FCSTD DOCUMENT  (FreeCAD 0.18R16131 (Git))
Label: SomeFaceJustLayer
License: All rights reserved
LicenseURL: http://en.wikipedia.org/wiki/All_rights_reserved
objects: Sketcher::SketchObject×1
note: 1 computed .brp shape members not serialized (recipe doc carries the construction recipe); baked Part::Feature solids carry a one-line shape summary decoded from their .brp

FEATURE [Sketcher::SketchObject] Sketch
  sketch-geometry (11):
    g0: LineSegment StartX=-16.4573 StartY=10.8332 StartZ=0 EndX=-15.7927 EndY=19.2026 EndZ=0
    g1: LineSegment StartX=-15.7927 StartY=19.2026 StartZ=0 EndX=-22.7085 EndY=23.9628 EndZ=0
    g2: LineSegment StartX=-22.7085 StartY=23.9628 StartZ=0 EndX=-30.2889 EndY=20.3537 EndZ=0
    g3: LineSegment StartX=-30.2889 StartY=20.3537 StartZ=0 EndX=-30.9535 EndY=11.9843 EndZ=0
    g4: LineSegment StartX=-30.9535 StartY=11.9843 StartZ=0 EndX=-24.0377 EndY=7.22407 EndZ=0
    g5: LineSegment StartX=-24.0377 StartY=7.22407 StartZ=0 EndX=-16.4573 EndY=10.8332 EndZ=0
    g6: Circle [constr] CenterX=-23.3731 CenterY=15.5935 CenterZ=0 NormalX=0 NormalY=0 NormalZ=1 AngleXU=0 Radius=8.39573
    g7: ArcOfCircle CenterX=-40.1686 CenterY=13.6448 CenterZ=0 NormalX=0 NormalY=0 NormalZ=1 AngleXU=0 Radius=15.6279 StartAngle=1.5708 EndAngle=4.71239
    g8: ArcOfCircle CenterX=6.8872 CenterY=13.6448 CenterZ=0 NormalX=0 NormalY=0 NormalZ=1 AngleXU=0 Radius=15.6279 StartAngle=4.71239 EndAngle=7.85398
    g9: LineSegment StartX=-40.1686 StartY=-1.98313 StartZ=0 EndX=6.8872 EndY=-1.98313 EndZ=0
    g10: LineSegment StartX=-40.1686 StartY=29.2728 StartZ=0 EndX=6.8872 EndY=29.2728 EndZ=0
  constraints (19):
    c: Coincident(g0,g1)
    c: Coincident(g1,g2)
    c: Coincident(g2,g3)
    c: Coincident(g3,g4)
    c: Coincident(g4,g5)
    c: Coincident(g5,g0)
    c: Equal(g0, g1-g5) x5
    c: PointOnObject(g0,g6)
    c: PointOnObject(g1,g6)
    c: PointOnObject(g2,g6)
    c: PointOnObject(g3,g6)
    c: PointOnObject(g4,g6)
    c: PointOnObject(g5,g6)
    c: Tangent(g7,g10) = 1.5708
    c: Tangent(g7,g9) = -1.5708
    c: Tangent(g9,g8) = -1.5708
    c: Tangent(g10,g8) = 1.5708
    c: Horizontal(g9)
    c: Equal(g7,g8)
